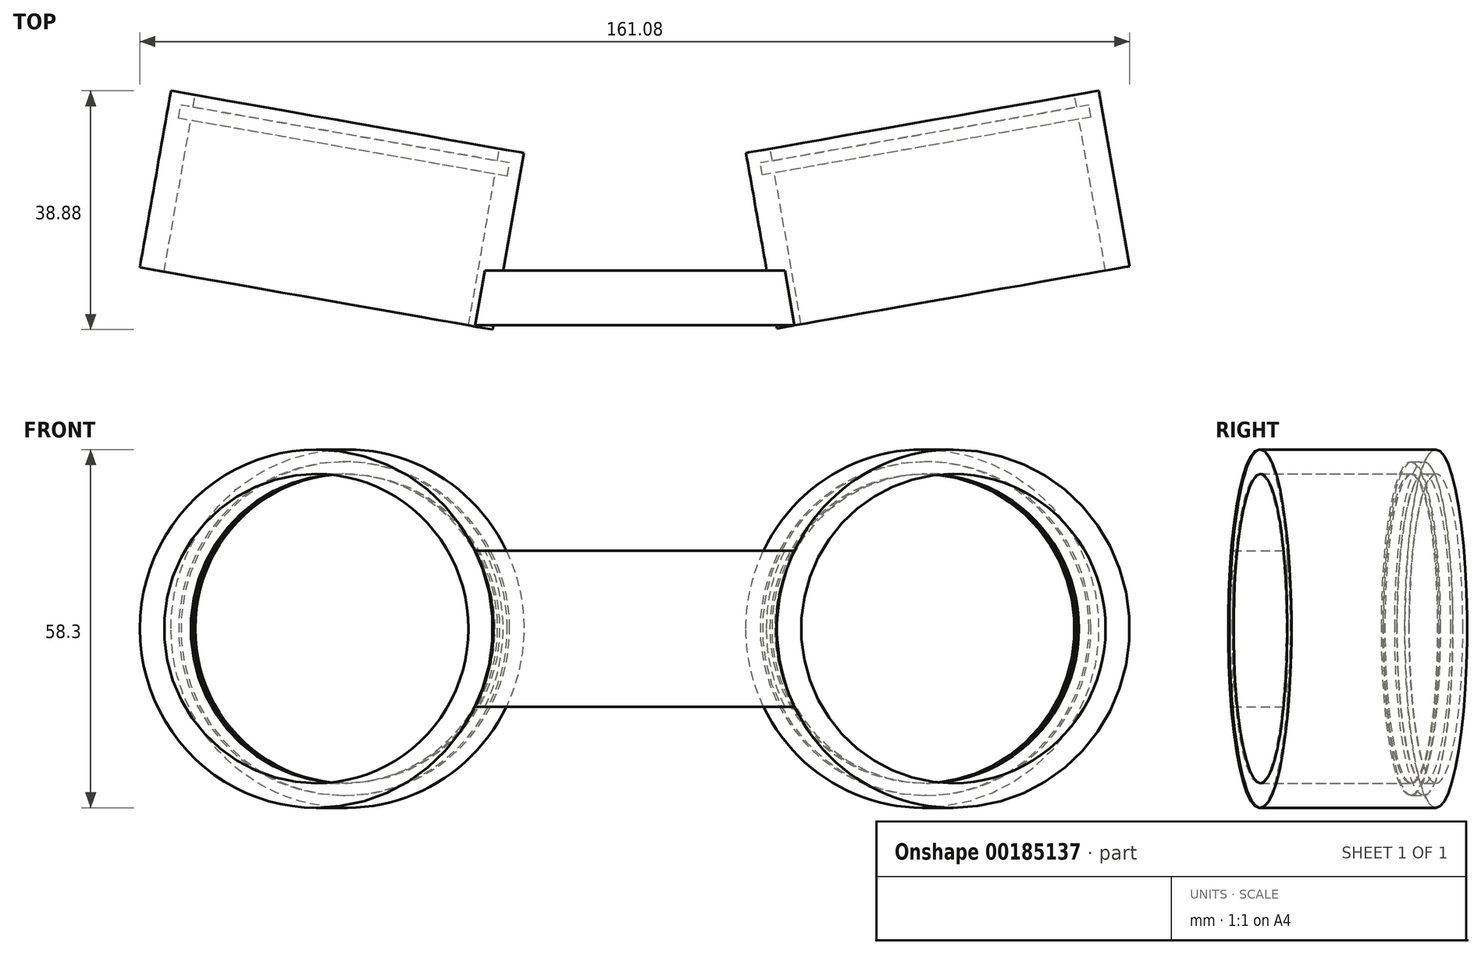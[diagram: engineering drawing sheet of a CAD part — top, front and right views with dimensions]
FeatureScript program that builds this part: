
annotation { "Feature Type Name" : "Feature", "Feature Type Description" : "" }
export const myFeature = defineFeature(function(context is Context, id is Id, definition is map)
    precondition{}
    {
        {
            var Q0;
            Q0=qCreatedBy(makeId("Front.planeOp"),FACE);
            var sketch = newSketch(context, id + "F0", { "sketchPlane" : qUnion([Q0])});
            skLineSegment(sketch, "E0", {"start": v(0, 36.22) * mm, "end": v(0, -35.6) * mm});
            skSolve(sketch);
        }
        {
            var Q0;
            Q0=sQuery(id+"F0.wireOp",EDGE,"E0");
            var Q1;
            Q1=qCreatedBy(makeId("Front.planeOp"),FACE);
            cPlane(context, id + "F1", {"entities" : qUnion([Q0, Q1]), "cplaneType" : CPlaneType.LINE_ANGLE, "offset" : 25.4 * mm, "angle" : 10 * degree, "width" : 152.4 * mm, "height" : 152.4 * mm});
        }
        {
            var Q0;
            Q0=qCreatedBy(id+"F1.planeOp",FACE);
            var sketch = newSketch(context, id + "F2", { "sketchPlane" : qUnion([Q0])});
            skCircle(sketch, "E1", {"center": v(47.5, 0) * mm, "radius": 25.15 * mm});
            skCircle(sketch, "E2", {"center": v(47.5, 0) * mm, "radius": 29.15 * mm});
            skSolve(sketch);
        }
        {
            var Q0;
            Q0=makeQuery(id+"F2.imprint","IMPRINT",FACE,{"disambiguationData":[TD([[makeQuery(id+"F2.imprint","IMPRINT",EDGE,{"derivedFrom":sQuery(id+"F2.wireOp",EDGE,"E1")}),-1.0]])]});
            extrude(context, id + "F3", {"entities" : qUnion([Q0]), "oppositeDirection" : true, "depth" : 2 * mm});
        }
        {
            var Q0;
            Q0=makeQuery(id+"F3.opExtrude","CAP_FACE",FACE,{"disambiguationData":[OSD([sQuery(id+"F2.wireOp",EDGE,"E1"),sQuery(id+"F2.wireOp",EDGE,"E2")])],"isStart":false});
            var sketch = newSketch(context, id + "F4", { "sketchPlane" : qUnion([Q0])});
            skCircle(sketch, "E3.0", {"center": v(-47.5, 0) * mm, "radius": 29.15 * mm});
            skCircle(sketch, "E4.0", {"center": v(-47.5, 0) * mm, "radius": 25.15 * mm});
            skCircle(sketch, "E5", {"center": v(-47.5, 0) * mm, "radius": 27.15 * mm});
            skSolve(sketch);
        }
        {
            var Q0;
            Q0=makeQuery(id+"F4.imprint","IMPRINT",FACE,{"disambiguationData":[TD([[makeQuery(id+"F4.imprint","IMPRINT",EDGE,{"derivedFrom":sQuery(id+"F4.wireOp",EDGE,"E3.0")}),-1.0]])]});
            extrude(context, id + "F5", {"entities" : qUnion([Q0]), "operationType" : NewBodyOperationType.ADD, "depth" : 2.2 * mm});
        }
        {
            var Q0;
            Q0=makeQuery(id+"F5.opExtrude","CAP_FACE",FACE,{"disambiguationData":[OSD([sQuery(id+"F4.wireOp",EDGE,"E3.0"),sQuery(id+"F4.wireOp",EDGE,"E5")])],"isStart":false});
            var sketch = newSketch(context, id + "F6", { "sketchPlane" : qUnion([Q0])});
            skCircle(sketch, "E6.0", {"center": v(-47.5, 0) * mm, "radius": 25.15 * mm});
            skCircle(sketch, "E7.0", {"center": v(-47.5, 0) * mm, "radius": 29.15 * mm});
            skSolve(sketch);
        }
        {
            var Q0;
            Q0=makeQuery(id+"F6.imprint","IMPRINT",FACE,{"disambiguationData":[TD([[makeQuery(id+"F6.imprint","IMPRINT",EDGE,{"derivedFrom":sQuery(id+"F6.wireOp",EDGE,"E6.0")}),-1.0]])]});
            var Q1;
            Q1=makeQuery(id+"F6.imprint","IMPRINT",FACE,{"disambiguationData":[TD([[makeQuery(id+"F6.imprint","IMPRINT",EDGE,{"derivedFrom":sQuery(id+"F6.wireOp",EDGE,"E7.0")}),-1.0]])]});
            extrude(context, id + "F7", {"entities" : qUnion([Q0, Q1]), "operationType" : NewBodyOperationType.ADD, "depth" : 5 * mm});
        }
        {
            var Q0;
            Q0=sQuery(id+"F0.wireOp",EDGE,"E0");
            var Q1;
            Q1=qCreatedBy(makeId("Front.planeOp"),FACE);
            cPlane(context, id + "F8", {"entities" : qUnion([Q0, Q1]), "cplaneType" : CPlaneType.LINE_ANGLE, "offset" : 25.4 * mm, "angle" : 350 * degree, "width" : 152.4 * mm, "height" : 152.4 * mm});
        }
        {
            var Q0;
            Q0=qCreatedBy(id+"F8.planeOp",FACE);
            var sketch = newSketch(context, id + "F9", { "sketchPlane" : qUnion([Q0])});
            skCircle(sketch, "E8", {"center": v(-47.5, 0) * mm, "radius": 29.15 * mm});
            skCircle(sketch, "E9", {"center": v(-47.5, 0) * mm, "radius": 25.15 * mm});
            skSolve(sketch);
        }
        {
            var Q0;
            Q0=makeQuery(id+"F9.imprint","IMPRINT",FACE,{"disambiguationData":[TD([[makeQuery(id+"F9.imprint","IMPRINT",EDGE,{"derivedFrom":sQuery(id+"F9.wireOp",EDGE,"E8")}),1.0]])]});
            extrude(context, id + "F10", {"entities" : qUnion([Q0]), "oppositeDirection" : true, "depth" : 2 * mm});
        }
        {
            var Q0;
            Q0=makeQuery(id+"F10.opExtrude","CAP_FACE",FACE,{"disambiguationData":[OSD([sQuery(id+"F9.wireOp",EDGE,"E8"),sQuery(id+"F9.wireOp",EDGE,"E9")])],"isStart":false});
            var sketch = newSketch(context, id + "F11", { "sketchPlane" : qUnion([Q0])});
            skCircle(sketch, "E10.0", {"center": v(47.5, 0) * mm, "radius": 25.15 * mm});
            skCircle(sketch, "E11.0", {"center": v(47.5, 0) * mm, "radius": 29.15 * mm});
            skCircle(sketch, "E12", {"center": v(47.5, 0) * mm, "radius": 27.15 * mm});
            skSolve(sketch);
        }
        {
            var Q0;
            Q0=makeQuery(id+"F11.imprint","IMPRINT",FACE,{"disambiguationData":[TD([[makeQuery(id+"F11.imprint","IMPRINT",EDGE,{"derivedFrom":sQuery(id+"F11.wireOp",EDGE,"E11.0")}),-1.0]])]});
            extrude(context, id + "F12", {"entities" : qUnion([Q0]), "operationType" : NewBodyOperationType.ADD, "depth" : 2 * mm});
        }
        {
            var Q0;
            Q0=makeQuery(id+"F12.opExtrude","CAP_FACE",FACE,{"disambiguationData":[OSD([sQuery(id+"F11.wireOp",EDGE,"E11.0"),sQuery(id+"F11.wireOp",EDGE,"E12")])],"isStart":false});
            var sketch = newSketch(context, id + "F13", { "sketchPlane" : qUnion([Q0])});
            skCircle(sketch, "E13.0", {"center": v(47.5, 0) * mm, "radius": 25.15 * mm});
            skCircle(sketch, "E14.0", {"center": v(47.5, 0) * mm, "radius": 29.15 * mm});
            skSolve(sketch);
        }
        {
            var Q0;
            Q0=makeQuery(id+"F13.imprint","IMPRINT",FACE,{"disambiguationData":[TD([[makeQuery(id+"F13.imprint","IMPRINT",EDGE,{"derivedFrom":sQuery(id+"F13.wireOp",EDGE,"E14.0")}),-1.0]])]});
            var Q1;
            Q1=makeQuery(id+"F13.imprint","IMPRINT",FACE,{"disambiguationData":[TD([[makeQuery(id+"F13.imprint","IMPRINT",EDGE,{"derivedFrom":sQuery(id+"F13.wireOp",EDGE,"E13.0")}),-1.0]])]});
            extrude(context, id + "F14", {"entities" : qUnion([Q0, Q1]), "operationType" : NewBodyOperationType.ADD, "depth" : 5 * mm});
        }
        {
            var Q0;
            Q0=makeQuery(id+"F7.opExtrude","CAP_FACE",FACE,{"disambiguationData":[OSD([sQuery(id+"F6.wireOp",EDGE,"E6.0"),sQuery(id+"F6.wireOp",EDGE,"E7.0")])],"isStart":false});
            extrude(context, id + "F15", {"entities" : qUnion([Q0]), "operationType" : NewBodyOperationType.ADD, "depth" : 20 * mm});
        }
        {
            var Q0;
            Q0=makeQuery(id+"F14.opExtrude","CAP_FACE",FACE,{"disambiguationData":[OSD([sQuery(id+"F13.wireOp",EDGE,"E13.0"),sQuery(id+"F13.wireOp",EDGE,"E14.0")])],"isStart":false});
            extrude(context, id + "F16", {"entities" : qUnion([Q0]), "operationType" : NewBodyOperationType.ADD, "depth" : 20 * mm});
        }
        {
            var Q0;
            Q0=qCreatedBy(makeId("Right.planeOp"),FACE);
            var sketch = newSketch(context, id + "F17", { "sketchPlane" : qUnion([Q0])});
            skEllipse(sketch, "E15.0", {"center": v(-20.5, 0) * mm, "majorRadius": 29.15 * mm, "minorRadius": 5.06 * mm, "majorAxis": v(0, -1)});
            skEllipse(sketch, "E16.0", {"center": v(-20.31, 0) * mm, "majorRadius": 29.15 * mm, "minorRadius": 5.06 * mm, "majorAxis": v(0, -1)});
            skLineSegment(sketch, "E17.bottom", {"start": v(-24.87, 12.7) * mm, "end": v(-15.95, 12.7) * mm});
            skLineSegment(sketch, "E17.top", {"start": v(-24.87, -12.7) * mm, "end": v(-15.95, -12.7) * mm});
            skLineSegment(sketch, "E17.left", {"start": v(-24.87, 12.7) * mm, "end": v(-24.87, -12.7) * mm});
            skLineSegment(sketch, "E17.right", {"start": v(-15.95, 12.7) * mm, "end": v(-15.95, -12.7) * mm});
            skSolve(sketch);
        }
        {
            var Q0;
            Q0=makeQuery(id+"F17.imprint","IMPRINT",FACE,{"disambiguationData":[TD([[makeQuery(id+"F17.imprint","IMPRINT",EDGE,{"derivedFrom":sQuery(id+"F17.wireOp",EDGE,"E17.bottom")}),-1.0]])]});
            extrude(context, id + "F18", {"entities" : qUnion([Q0]), "operationType" : NewBodyOperationType.ADD, "endBound" : BoundingType.UP_TO_NEXT, "depth" : 25.4 * mm});
        }
        {
            var Q0;
            Q0=makeQuery(id+"F17.imprint","IMPRINT",FACE,{"disambiguationData":[TD([[makeQuery(id+"F17.imprint","IMPRINT",EDGE,{"derivedFrom":sQuery(id+"F17.wireOp",EDGE,"E17.bottom")}),-1.0]])]});
            extrude(context, id + "F19", {"entities" : qUnion([Q0]), "operationType" : NewBodyOperationType.ADD, "endBound" : BoundingType.UP_TO_NEXT, "oppositeDirection" : true, "depth" : 25.4 * mm});
        }
    });
